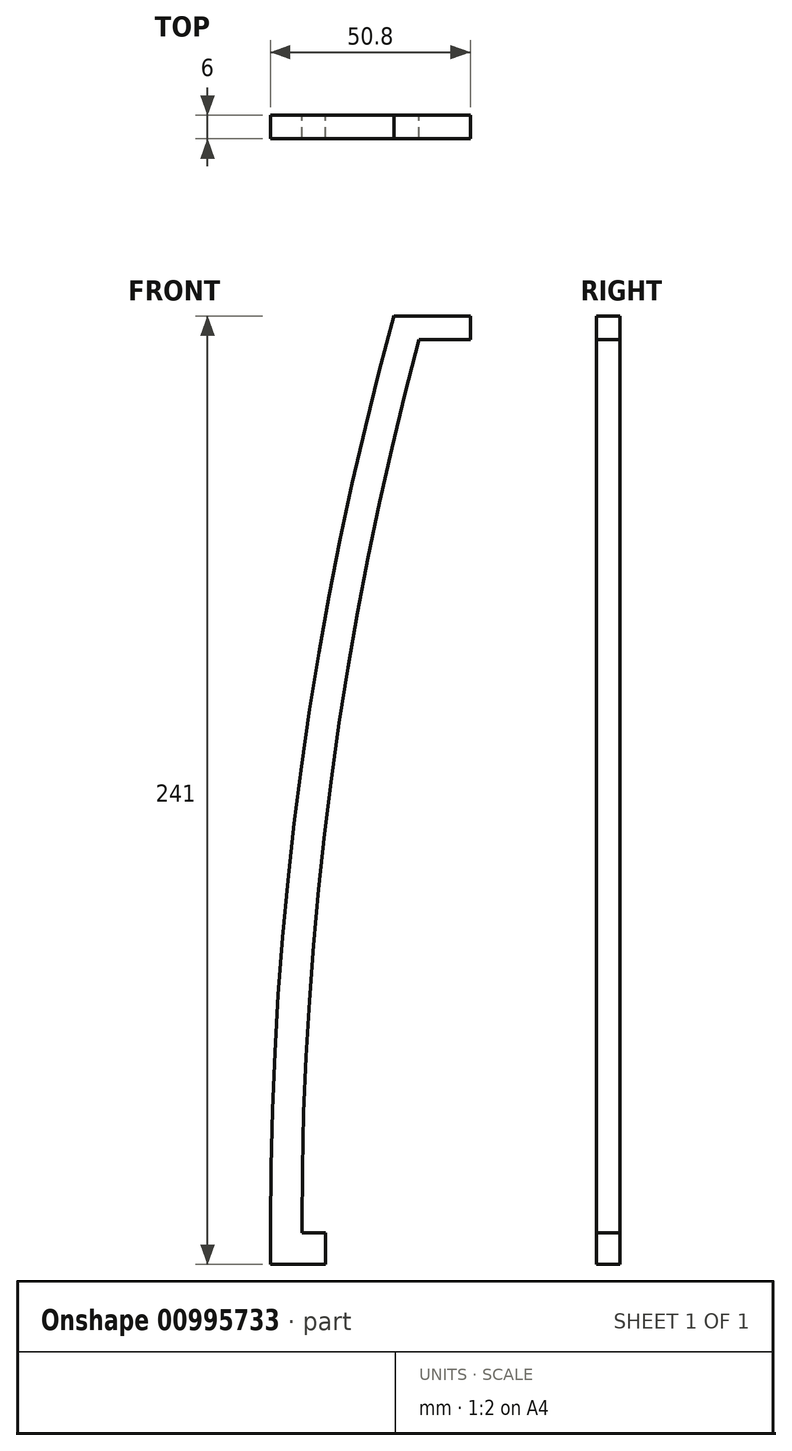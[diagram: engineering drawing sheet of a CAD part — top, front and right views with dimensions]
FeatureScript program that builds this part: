
annotation { "Feature Type Name" : "Feature", "Feature Type Description" : "" }
export const myFeature = defineFeature(function(context is Context, id is Id, definition is map)
    precondition{}
    {
        {
            var Q0;
            Q0=qCreatedBy(makeId("Front.planeOp"),FACE);
            var sketch = newSketch(context, id + "F0", { "sketchPlane" : qUnion([Q0])});
            skLineSegment(sketch, "E0", {"start": v(-4.2, 235) * mm, "end": v(-17.2, 235) * mm});
            skLineSegment(sketch, "E1", {"start": v(-4.2, 241) * mm, "end": v(-23.56, 241) * mm});
            skLineSegment(sketch, "E2", {"start": v(-47, 0) * mm, "end": v(-47, 10) * mm});
            skLineSegment(sketch, "E3", {"start": v(-55, 0) * mm, "end": v(-55, 10) * mm});
            skLineSegment(sketch, "E4", {"start": v(-47, 0) * mm, "end": v(-55, 0) * mm});
            skArc(sketch, "E5", {"start": v(-17.2, 235) * mm, "mid": v(-39.52, 123.48) * mm, "end": v(-47, 10) * mm});
            skArc(sketch, "E6", {"start": v(-23.56, 241) * mm, "mid": v(-47.1, 126.56) * mm, "end": v(-55, 10) * mm});
            skLineSegment(sketch, "E7", {"start": v(-4.2, 241) * mm, "end": v(-4.2, 235) * mm});
            skSolve(sketch);
        }
        {
            var Q0;
            Q0=makeQuery(id+"F0.imprint","IMPRINT",FACE,{"disambiguationData":[TD([[makeQuery(id+"F0.imprint","IMPRINT",EDGE,{"derivedFrom":sQuery(id+"F0.wireOp",EDGE,"E0")}),-1.0]])]});
            extrude(context, id + "F1", {"entities" : qUnion([Q0]), "depth" : 6 * mm, "offsetDistance" : 25 * mm});
        }
        {
            var Q0;
            Q0=makeQuery(id+"F1.opExtrude","SWEPT_FACE",FACE,{"disambiguationData":[OSD([sQuery(id+"F0.wireOp",EDGE,"E2")])]});
            extrude(context, id + "F2", {"entities" : qUnion([Q0]), "operationType" : NewBodyOperationType.ADD, "depth" : 6 * mm, "offsetDistance" : 25 * mm});
        }
        {
            var Q0;
            Q0=makeQuery(id+"F2.opExtrude","SWEPT_FACE",FACE,{"disambiguationData":[OSD([sQuery(id+"F0.wireOp",EDGE,"E2"),sQuery(id+"F0.wireOp",EDGE,"E5")])]});
            extrude(context, id + "F3", {"entities" : qUnion([Q0]), "operationType" : NewBodyOperationType.REMOVE, "oppositeDirection" : true, "depth" : 2 * mm, "offsetDistance" : 25 * mm});
        }
    });
